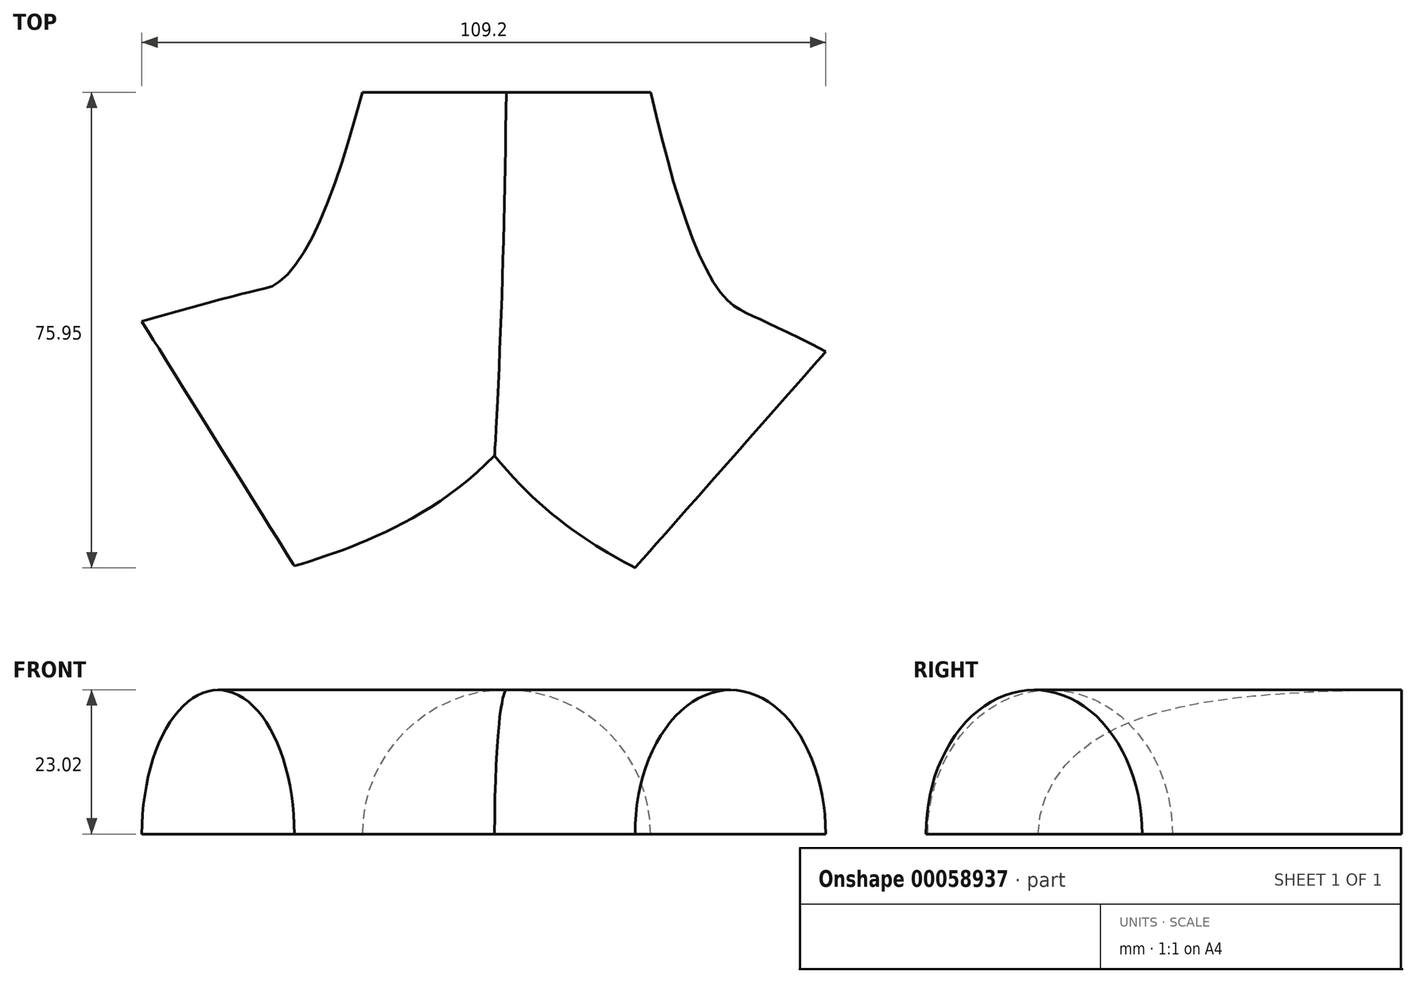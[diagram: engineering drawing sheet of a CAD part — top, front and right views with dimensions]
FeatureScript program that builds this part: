
annotation { "Feature Type Name" : "Feature", "Feature Type Description" : "" }
export const myFeature = defineFeature(function(context is Context, id is Id, definition is map)
    precondition{}
    {
        {
            var Q0;
            Q0=qCreatedBy(makeId("Front.planeOp"),FACE);
            var sketch = newSketch(context, id + "F0", { "sketchPlane" : qUnion([Q0])});
            skArc(sketch, "E0", {"start": v(23.02, 0) * mm, "mid": v(0, 23.02) * mm, "end": v(-23.02, 0) * mm});
            skLineSegment(sketch, "E1", {"start": v(-23.02, 0) * mm, "end": v(23.02, 0) * mm});
            skSolve(sketch);
        }
        {
            var Q0;
            Q0=qCreatedBy(makeId("Top.planeOp"),FACE);
            var sketch = newSketch(context, id + "F1", { "sketchPlane" : qUnion([Q0])});
            skFitSpline(sketch, "E2", {"points": [v(0, 0) * mm, v(-17.7, -41.96) * mm, v(-46.03, -56.12) * mm], "startDerivative": vector(-24.34, -89.44) * mm, "endDerivative": vector(-69.08, -20.73) * mm});
            skFitSpline(sketch, "E3", {"points": [v(0, 0) * mm, v(15.23, -43.11) * mm, v(35.76, -58.7) * mm], "startDerivative": vector(20.6, -86.66) * mm, "endDerivative": vector(52.44, -27.93) * mm});
            skSolve(sketch);
        }
        {
            var Q0;
            Q0=makeQuery(id+"F0.imprint","IMPRINT",FACE,{"disambiguationData":[TD([[makeQuery(id+"F0.imprint","IMPRINT",EDGE,{"derivedFrom":sQuery(id+"F0.wireOp",EDGE,"E0")}),1.0]])]});
            var Q1;
            Q1=sQuery(id+"F1.wireOp",EDGE,"E2");
            sweep(context, id + "F2", {"profiles" : qUnion([Q0]), "path" : qUnion([Q1])});
        }
        {
            var Q0;
            Q0=makeQuery(id+"F2.opSweep","CAP_FACE",FACE,{"disambiguationData":[OSD([sQuery(id+"F0.wireOp",EDGE,"E0"),sQuery(id+"F0.wireOp",EDGE,"E1"),sQuery(id+"F1.wireOp",VERTEX,"E2.start")])],"isStart":true});
            var Q1;
            Q1=sQuery(id+"F1.wireOp",EDGE,"E3");
            sweep(context, id + "F3", {"operationType" : NewBodyOperationType.ADD, "profiles" : qUnion([Q0]), "path" : qUnion([Q1])});
        }
    });
